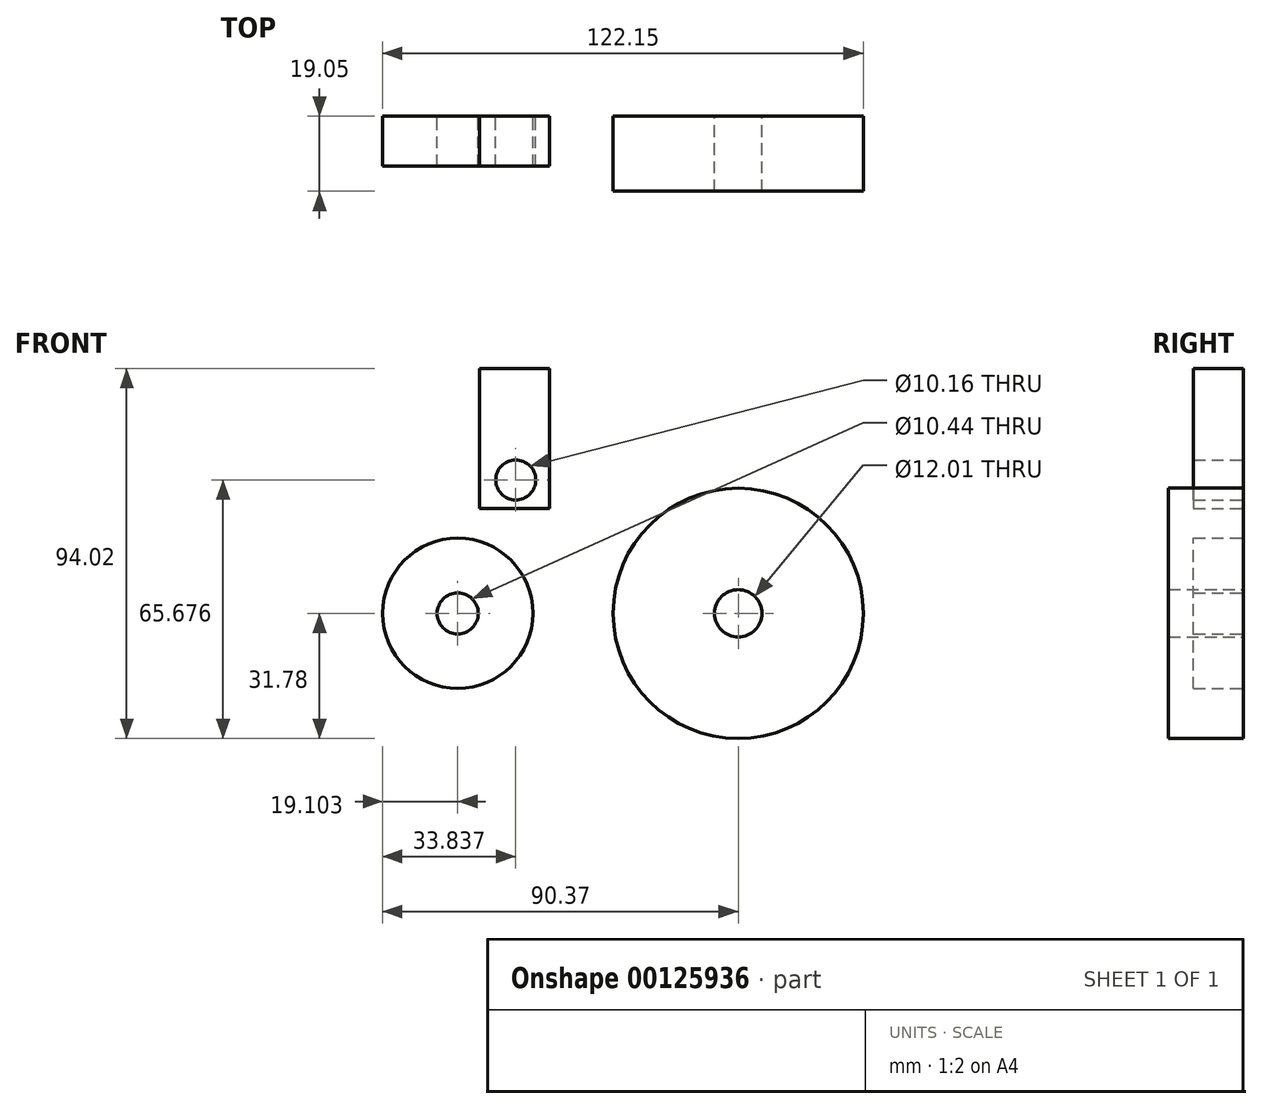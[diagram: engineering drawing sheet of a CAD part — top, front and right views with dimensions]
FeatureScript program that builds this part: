
annotation { "Feature Type Name" : "Feature", "Feature Type Description" : "" }
export const myFeature = defineFeature(function(context is Context, id is Id, definition is map)
    precondition{}
    {
        {
            var Q0;
            Q0=qCreatedBy(makeId("Front.planeOp"),FACE);
            var sketch = newSketch(context, id + "F0", { "sketchPlane" : qUnion([Q0])});
            skCircle(sketch, "E0", {"center": v(0, 0) * mm, "radius": 31.78 * mm});
            skCircle(sketch, "E1", {"center": v(0, 0) * mm, "radius": 6 * mm});
            skSolve(sketch);
        }
        {
            var Q0;
            Q0=qSketchRegion(id+"F0",true);
            extrude(context, id + "F1", {"entities" : qUnion([Q0]), "depth" : 19.05 * mm});
        }
        {
            var Q0;
            Q0=qCreatedBy(makeId("Front.planeOp"),FACE);
            var sketch = newSketch(context, id + "F2", { "sketchPlane" : qUnion([Q0])});
            skCircle(sketch, "E2", {"center": v(-71.27, 0) * mm, "radius": 19.1 * mm});
            skCircle(sketch, "E3", {"center": v(-71.27, 0) * mm, "radius": 5.22 * mm});
            skSolve(sketch);
        }
        {
            var Q0;
            Q0=qSketchRegion(id+"F2",true);
            extrude(context, id + "F3", {"entities" : qUnion([Q0]), "depth" : 12.7 * mm});
        }
        {
            var Q0;
            Q0=qCreatedBy(makeId("Front.planeOp"),FACE);
            var sketch = newSketch(context, id + "F4", { "sketchPlane" : qUnion([Q0])});
            skLineSegment(sketch, "E4.bottom", {"start": v(-65.78, 62.24) * mm, "end": v(-48, 62.24) * mm});
            skLineSegment(sketch, "E4.top", {"start": v(-65.78, 26.68) * mm, "end": v(-48, 26.68) * mm});
            skLineSegment(sketch, "E4.left", {"start": v(-65.78, 62.24) * mm, "end": v(-65.78, 26.68) * mm});
            skLineSegment(sketch, "E4.right", {"start": v(-48, 62.24) * mm, "end": v(-48, 26.68) * mm});
            skLineSegment(sketch, "E5", {"start": v(-65.78, 26.68) * mm, "end": v(-56.9, 26.68) * mm});
            skCircle(sketch, "E6", {"center": v(-56.53, 33.9) * mm, "radius": 5.08 * mm});
            skLineSegment(sketch, "E7", {"start": v(-56.9, 26.68) * mm, "end": v(-56.53, 62.24) * mm});
            skPoint(sketch, "E7.endSnap0", {"position": v(-56.9, 62.24) * mm});
            skSolve(sketch);
        }
        {
            var Q0;
            Q0=qSketchRegion(id+"F4",true);
            extrude(context, id + "F5", {"entities" : qUnion([Q0]), "depth" : 12.7 * mm});
        }
    });
